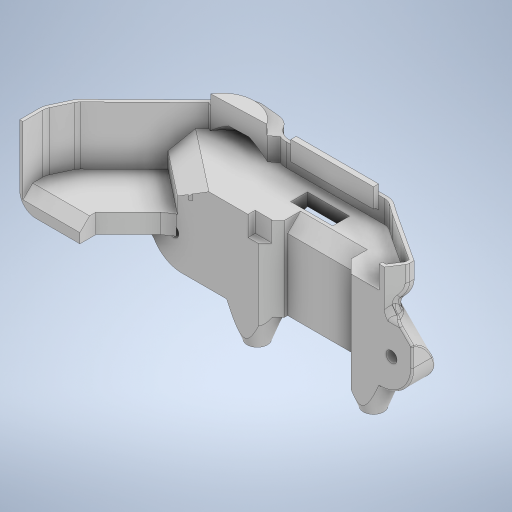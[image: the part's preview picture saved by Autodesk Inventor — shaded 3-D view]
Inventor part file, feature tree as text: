
AUTODESK INVENTOR PART (.ipt)
format: ipt  version: 2023.4 (Build 274418000, 418)  size: 1,295,360 bytes
history: native  units: mm
features: extrude x15, sketch x15, chamfer x12, fillet x10, projected_geometry x9, reference x4, other x4, thicken_offset x3, plane x1
ambient origin geometry x8: Origin, YZ Plane, XZ Plane, XY Plane, X Axis, Y Axis, Z Axis, Center Point
bodies: Solid1 (feature_tree)
feature tree (73):
  extrude  "Extrusion1"  Depth=20.0mm
  extrude  "Extrusion2"  Depth=3.4mm
  extrude  "Extrusion3"  Depth=10.0mm TaperAngle=0.0deg
  extrude  "Extrusion4"  Depth=3.3mm
  chamfer  "Chamfer1"  [1 undecoded]
  chamfer  "Chamfer2"  Distance=10.0mm
  extrude  "Extrusion5"  Depth=10.0mm
  fillet  "Fillet1"  Radius=5.0mm
  extrude  "Extrusion6"  Depth=10.0mm
  plane  "Work Plane1"
  extrude  "Extrusion7"  Depth=1.0mm TaperAngle=0.0deg
  extrude  "Extrusion8"  Depth=5.0mm TaperAngle=45.0deg
  chamfer  "Chamfer4"  Distance=4.0mm Angle=45.0deg
  chamfer  "Chamfer5"  Distance=4.0mm Angle=45.0deg
  chamfer  "Chamfer6"  Distance=4.0mm Angle=45.0deg
  chamfer  "Chamfer7"  Distance=10.0mm
  fillet  "Fillet2"  Radius=7.0mm
  fillet  "Fillet3"  Radius=5.0mm
  fillet  "Fillet4"  Radius=5.0mm
  fillet  "Fillet5"  Radius=0.5mm
  fillet  "Fillet6"  Radius=2.0mm
  fillet  "Fillet7"  Radius=2.0mm
  fillet  "Fillet8"  Radius=2.0mm
  fillet  "Fillet9"  [1 undecoded]
  fillet  "Fillet10"  Radius=1.0mm
  extrude  "Extrusion9"  Depth=10.0mm TaperAngle=0.0deg
  extrude  "Extrusion10"  Depth=10.0mm TaperAngle=0.0deg
  extrude  "Extrusion11"  TaperAngle=0.0deg  [1 undecoded]
  extrude  "Extrusion12"  Depth=10.0mm TaperAngle=45.0deg
  chamfer  "Chamfer8"  [1 undecoded]
  extrude  "Extrusion13"  Depth=10.0mm TaperAngle=45.0deg
  chamfer  "Chamfer9"  Distance=6.0mm
  extrude  "Extrusion14"  Depth=10.0mm TaperAngle=45.0deg
  chamfer  "Chamfer10"  Distance=4.0mm Angle=45.0deg
  chamfer  "Chamfer11"  Distance=6.0mm
  extrude  "Extrusion15"  Depth=10.0mm TaperAngle=45.0deg
  chamfer  "Chamfer12"  Distance=1.0mm Angle=45.0deg
  chamfer  "Chamfer13"  Distance=0.2mm
  thicken_offset  "Thicken1"
  thicken_offset  "Thicken2"
  thicken_offset  "Thicken3"
  sketch  "Sketch1"  dims[d0=80.0mm d1=20.0mm]
  sketch  "Sketch2"  dims[d2=8.0mm d3=0.0mm d4=3.4mm]
  sketch  "Sketch3"  dims[d5=3.4mm d6=10.0mm d7=0.0mm]
  sketch  "Sketch4"  dims[d8=36.0mm d9=3.3mm]
  sketch  "Sketch5"  dims[d10=3.3mm]
  sketch  "Sketch6"  dims[d11=16.0mm]
  projected_geometry  "Projected Loop1"
  sketch  "Sketch7"  dims[d12=4.0mm]
  projected_geometry  "Projected Loop2"
  sketch  "Sketch8"  dims[d13=4.0mm d14=0.0mm d15=0.0mm]
  projected_geometry  "Projected Loop3"
  sketch  "Sketch9"  dims[d16=1.5mm]
  projected_geometry  "Projected Loop4"
  sketch  "Sketch10"  dims[d17=1.5mm d18=10.0mm d19=0.0mm]
  projected_geometry  "Projected Loop5"
  sketch  "Sketch11"  dims[d20=10.0mm d21=2.0mm d22=3.490659mm d23=10.0mm d24=2.0mm d25=3.490659mm d29=5.0mm]
  projected_geometry  "Projected Loop6"
  sketch  "Sketch12"  dims[d30=0.0mm d31=0.0mm d32=10.0mm]
  sketch  "Sketch13"  dims[d33=1.0mm d34=0.0mm d35=1.0mm d36=0.0mm]
  reference  "Reference6"
  reference  "Reference7"
  sketch  "Sketch14"  dims[d37=12.0mm d38=0.0mm d39=5.0mm d40=2.0mm d41=45.0deg d42=4.0mm d43=2.0mm d44=45.0deg d45=4.0mm d46=2.0mm d47=45.0deg d48=4.0mm d49=2.0mm d50=45.0deg]
  reference  "Reference8"
  reference  "Reference9"
  sketch  "Sketch15"  dims[d51=10.0mm d52=10.0mm d53=7.0mm d54=5.0mm d55=5.0mm d56=0.5mm d57=2.0mm d58=2.0mm d59=2.0mm d60=0.0mm d61=0.0mm d62=1.0mm d63=7.0mm d64=0.0mm d65=11.0mm d66=0.0mm d67=0.0mm d68=0.0mm d69=3.0mm d70=2.0mm d71=45.0deg d72=0.0mm d73=0.0mm d74=0.5mm d75=2.0mm d76=45.0deg d77=6.0mm d78=0.0mm d79=6.0mm d80=2.0mm d81=45.0deg d82=4.0mm d83=2.0mm d84=45.0deg d85=6.0mm d86=0.0mm d87=4.0mm d88=2.0mm d89=45.0deg d90=1.0mm d91=2.0mm d92=45.0deg d93=0.2mm d94=0.2mm d95=0.2mm d96=0.2mm d97=0.2mm d98=0.2mm]
  projected_geometry  "Projected Loop7"
  projected_geometry  "Projected Loop8"
  projected_geometry  "Projected Loop9"
  parser-record x1  (decoder bookkeeping rows leaked as tree rows — omitted from the tree; the rows remain in map.json)
  other  "MK3_Assembly.iam"
  other  "top_left:1"
  other  "separator_top_mid:1"
note: 4 required parameter values undecoded (feature->parameter linkage not recoverable at this tier; creation-order binding heuristic only, values carry confidence <= 0.55)
note: 1 file-system path scrubbed to <path> (originals preserved in map.json)
